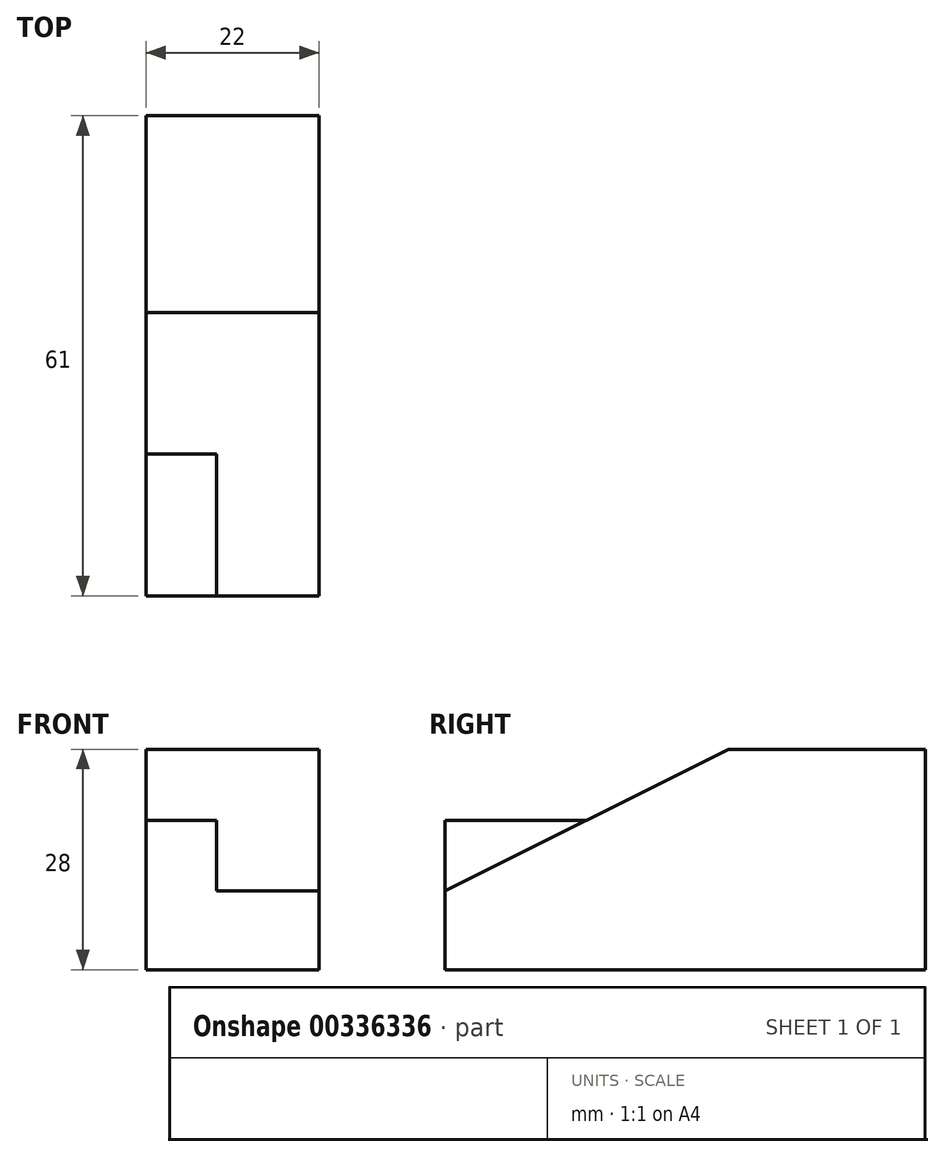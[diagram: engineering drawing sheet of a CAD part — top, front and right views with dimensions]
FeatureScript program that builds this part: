
annotation { "Feature Type Name" : "Feature", "Feature Type Description" : "" }
export const myFeature = defineFeature(function(context is Context, id is Id, definition is map)
    precondition{}
    {
        {
            var Q0;
            Q0=qCreatedBy(makeId("Top.planeOp"),FACE);
            var sketch = newSketch(context, id + "F0", { "sketchPlane" : qUnion([Q0])});
            skLineSegment(sketch, "E0.bottom", {"start": v(0, 0) * mm, "end": v(22, 0) * mm});
            skLineSegment(sketch, "E0.top", {"start": v(0, 61) * mm, "end": v(22, 61) * mm});
            skLineSegment(sketch, "E0.left", {"start": v(0, 0) * mm, "end": v(0, 61) * mm});
            skLineSegment(sketch, "E0.right", {"start": v(22, 0) * mm, "end": v(22, 61) * mm});
            skSolve(sketch);
        }
        {
            var Q0;
            Q0 = qSketchRegion(id + "F0", true);
            extrude(context, id + "F1", {"entities" : qUnion([Q0]), "depth" : 28 * mm});
        }
        {
            var Q0;
            Q0=makeQuery(id+"F1.opExtrude","SWEPT_FACE",FACE,{"disambiguationData":[OSD([sQuery(id+"F0.wireOp",EDGE,"E0.right")])]});
            var sketch = newSketch(context, id + "F2", { "sketchPlane" : qUnion([Q0])});
            skLineSegment(sketch, "E1", {"start": v(0, 28) * mm, "end": v(36, 28) * mm});
            skLineSegment(sketch, "E2", {"start": v(36, 28) * mm, "end": v(0, 10) * mm});
            skLineSegment(sketch, "E3", {"start": v(0, 10) * mm, "end": v(0, 28) * mm});
            skSolve(sketch);
        }
        {
            var Q0;
            Q0 = qSketchRegion(id + "F2", true);
            extrude(context, id + "F3", {"entities" : qUnion([Q0]), "operationType" : NewBodyOperationType.REMOVE, "endBound" : BoundingType.THROUGH_ALL, "oppositeDirection" : true, "depth" : 25 * mm});
        }
        {
            var Q0;
            Q0=makeQuery(id+"F1.opExtrude","SWEPT_FACE",FACE,{"disambiguationData":[OSD([sQuery(id+"F0.wireOp",EDGE,"E0.left")])]});
            var sketch = newSketch(context, id + "F4", { "sketchPlane" : qUnion([Q0])});
            skLineSegment(sketch, "E4", {"start": v(0, 10) * mm, "end": v(0, 19) * mm});
            skLineSegment(sketch, "E5", {"start": v(0, 19) * mm, "end": v(-18, 19) * mm});
            skLineSegment(sketch, "E6", {"start": v(-18, 19) * mm, "end": v(0, 10) * mm});
            skSolve(sketch);
        }
        {
            var Q0;
            Q0 = qSketchRegion(id + "F4", true);
            extrude(context, id + "F5", {"entities" : qUnion([Q0]), "operationType" : NewBodyOperationType.ADD, "oppositeDirection" : true, "depth" : 9 * mm});
        }
    });
